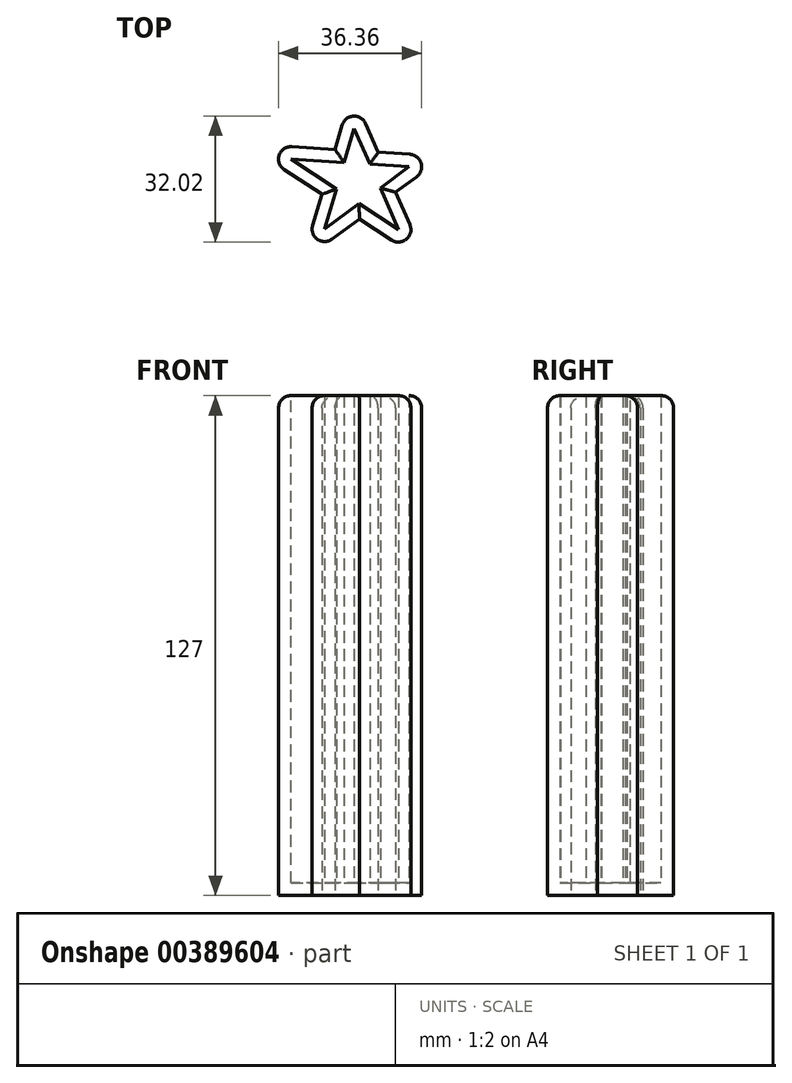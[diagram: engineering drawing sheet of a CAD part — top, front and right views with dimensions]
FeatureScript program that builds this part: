
annotation { "Feature Type Name" : "Feature", "Feature Type Description" : "" }
export const myFeature = defineFeature(function(context is Context, id is Id, definition is map)
    precondition{}
    {
        {
            var Q0;
            Q0=qCreatedBy(makeId("Top.planeOp"),FACE);
            var sketch = newSketch(context, id + "F0", { "sketchPlane" : qUnion([Q0])});
            skPoint(sketch, "E0.0.midPoint", {"position": v(12.38, 19.6) * mm});
            skLineSegment(sketch, "E1", {"start": v(-14.55, -17.02) * mm, "end": v(-9.55, -0.02) * mm});
            skLineSegment(sketch, "E2", {"start": v(-1.92, 25.94) * mm, "end": v(4.77, 10.66) * mm});
            skLineSegment(sketch, "E3", {"start": v(17.1, -17.5) * mm, "end": v(0, -6.29) * mm});
            skLineSegment(sketch, "E4", {"start": v(-29.17, 12.86) * mm, "end": v(-6.2, 11.37) * mm});
            skLineSegment(sketch, "E5", {"start": v(21.52, 9.58) * mm, "end": v(9.21, 0.5) * mm});
            skLineSegment(sketch, "E6.trimOffspring", {"start": v(-6.2, 11.37) * mm, "end": v(-1.92, 25.94) * mm});
            skLineSegment(sketch, "E7.trimOffspring", {"start": v(4.77, 10.66) * mm, "end": v(21.52, 9.58) * mm});
            skLineSegment(sketch, "E8.trimOffspring", {"start": v(9.21, 0.5) * mm, "end": v(17.1, -17.5) * mm});
            skLineSegment(sketch, "E9.trimOffspring", {"start": v(0, -6.29) * mm, "end": v(-14.55, -17.02) * mm});
            skLineSegment(sketch, "E10.trimOffspring", {"start": v(-9.55, -0.02) * mm, "end": v(-29.17, 12.86) * mm});
            skSolve(sketch);
        }
        {
            var Q0;
            Q0 = qSketchRegion(id + "F0", true);
            extrude(context, id + "F1", {"entities" : qUnion([Q0]), "endBound" : BoundingType.SYMMETRIC, "depth" : 127 * mm});
        }
        {
            var Q0;
            Q0=makeQuery(id+"F1.opExtrude","CAP_EDGE",EDGE,{"disambiguationData":[OSD([sQuery(id+"F0.wireOp",EDGE,"E10.trimOffspring")])],"isStart":false});
            var Q1;
            Q1=makeQuery(id+"F1.opExtrude","CAP_EDGE",EDGE,{"disambiguationData":[OSD([sQuery(id+"F0.wireOp",EDGE,"E4")])],"isStart":false});
            var Q2;
            Q2=makeQuery(id+"F1.opExtrude","CAP_EDGE",EDGE,{"disambiguationData":[OSD([sQuery(id+"F0.wireOp",EDGE,"E2")])],"isStart":false});
            var Q3;
            Q3=makeQuery(id+"F1.opExtrude","CAP_EDGE",EDGE,{"disambiguationData":[OSD([sQuery(id+"F0.wireOp",EDGE,"E6.trimOffspring")])],"isStart":false});
            var Q4;
            Q4=makeQuery(id+"F1.opExtrude","CAP_EDGE",EDGE,{"disambiguationData":[OSD([sQuery(id+"F0.wireOp",EDGE,"E7.trimOffspring")])],"isStart":false});
            var Q5;
            Q5=makeQuery(id+"F1.opExtrude","CAP_EDGE",EDGE,{"disambiguationData":[OSD([sQuery(id+"F0.wireOp",EDGE,"E5")])],"isStart":false});
            var Q6;
            Q6=makeQuery(id+"F1.opExtrude","CAP_EDGE",EDGE,{"disambiguationData":[OSD([sQuery(id+"F0.wireOp",EDGE,"E1")])],"isStart":false});
            var Q7;
            Q7=makeQuery(id+"F1.opExtrude","CAP_EDGE",EDGE,{"disambiguationData":[OSD([sQuery(id+"F0.wireOp",EDGE,"E9.trimOffspring")])],"isStart":false});
            var Q8;
            Q8=makeQuery(id+"F1.opExtrude","CAP_EDGE",EDGE,{"disambiguationData":[OSD([sQuery(id+"F0.wireOp",EDGE,"E3")])],"isStart":false});
            var Q9;
            Q9=makeQuery(id+"F1.opExtrude","CAP_EDGE",EDGE,{"disambiguationData":[OSD([sQuery(id+"F0.wireOp",EDGE,"E8.trimOffspring")])],"isStart":false});
            var Q10;
            Q10=makeQuery(id+"F1.opExtrude","SWEPT_EDGE",EDGE,{"disambiguationData":[OSD([sQuery(id+"F0.wireOp",EDGE,"E2"),sQuery(id+"F0.wireOp",EDGE,"E6.trimOffspring")])]});
            var Q11;
            Q11=makeQuery(id+"F1.opExtrude","SWEPT_EDGE",EDGE,{"disambiguationData":[OSD([sQuery(id+"F0.wireOp",EDGE,"E5"),sQuery(id+"F0.wireOp",EDGE,"E7.trimOffspring")])]});
            var Q12;
            Q12=makeQuery(id+"F1.opExtrude","SWEPT_EDGE",EDGE,{"disambiguationData":[OSD([sQuery(id+"F0.wireOp",EDGE,"E3"),sQuery(id+"F0.wireOp",EDGE,"E8.trimOffspring")])]});
            var Q13;
            Q13=makeQuery(id+"F1.opExtrude","SWEPT_EDGE",EDGE,{"disambiguationData":[OSD([sQuery(id+"F0.wireOp",EDGE,"E1"),sQuery(id+"F0.wireOp",EDGE,"E9.trimOffspring")])]});
            var Q14;
            Q14=makeQuery(id+"F1.opExtrude","SWEPT_EDGE",EDGE,{"disambiguationData":[OSD([sQuery(id+"F0.wireOp",EDGE,"E4"),sQuery(id+"F0.wireOp",EDGE,"E10.trimOffspring")])]});
            fillet(context, id + "F2", {"entities" : qUnion([Q0, Q1, Q2, Q3, Q4, Q5, Q6, Q7, Q8, Q9, Q10, Q11, Q12, Q13, Q14]), "radius" : 3.17 * mm, "tangentPropagation" : true, "allowEdgeOverflow" : false});
        }
        {
            var Q0;
            Q0=makeQuery(id+"F1.opExtrude","CAP_FACE",FACE,{"disambiguationData":[OSD([sQuery(id+"F0.wireOp",EDGE,"E1"),sQuery(id+"F0.wireOp",EDGE,"E2"),sQuery(id+"F0.wireOp",EDGE,"E3"),sQuery(id+"F0.wireOp",EDGE,"E4"),sQuery(id+"F0.wireOp",EDGE,"E5"),sQuery(id+"F0.wireOp",EDGE,"E6.trimOffspring"),sQuery(id+"F0.wireOp",EDGE,"E7.trimOffspring"),sQuery(id+"F0.wireOp",EDGE,"E8.trimOffspring"),sQuery(id+"F0.wireOp",EDGE,"E9.trimOffspring"),sQuery(id+"F0.wireOp",EDGE,"E10.trimOffspring")])],"isStart":false});
            shell(context, id + "F3", {"entities" : qUnion([Q0]), "thickness" : 3.17 * mm});
        }
    });
